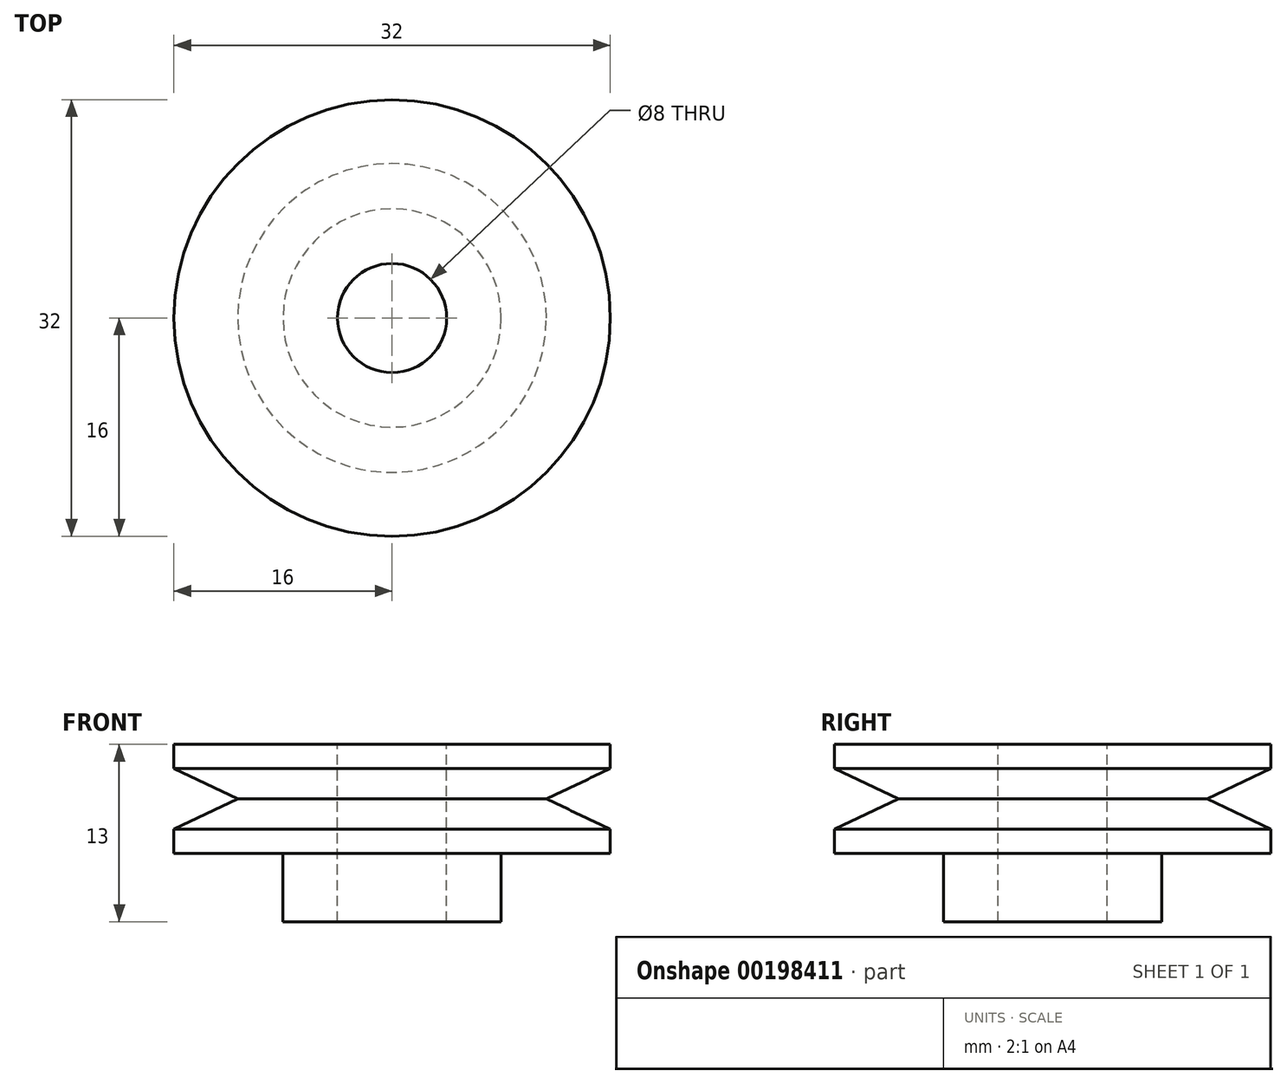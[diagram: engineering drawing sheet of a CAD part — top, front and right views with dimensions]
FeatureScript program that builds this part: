
annotation { "Feature Type Name" : "Feature", "Feature Type Description" : "" }
export const myFeature = defineFeature(function(context is Context, id is Id, definition is map)
    precondition{}
    {
        {
            var Q0;
            Q0=qCreatedBy(makeId("Front.planeOp"),FACE);
            var sketch = newSketch(context, id + "F0", { "sketchPlane" : qUnion([Q0])});
            skLineSegment(sketch, "E0", {"start": v(0, 0) * mm, "end": v(-8, 0) * mm});
            skLineSegment(sketch, "E1", {"start": v(-8, 0) * mm, "end": v(-8, 5) * mm});
            skLineSegment(sketch, "E2", {"start": v(-8, 5) * mm, "end": v(-16, 5) * mm});
            skLineSegment(sketch, "E3", {"start": v(-16, 5) * mm, "end": v(-16, 6.78) * mm});
            skLineSegment(sketch, "E4", {"start": v(-16, 13) * mm, "end": v(-8, 13) * mm});
            skLineSegment(sketch, "E5", {"start": v(0, 13) * mm, "end": v(0, 0) * mm});
            skLineSegment(sketch, "E6", {"start": v(-11.32, 9) * mm, "end": v(-16, 11.22) * mm});
            skPoint(sketch, "E6.startSnap0", {"position": v(-16, 9) * mm});
            skLineSegment(sketch, "E7.MirrorCS", {"start": v(-11.32, 9) * mm, "end": v(-16, 6.78) * mm});
            skPoint(sketch, "E8.orphan", {"position": v(-30.85, 18.27) * mm});
            skPoint(sketch, "E9.orphan", {"position": v(-30.85, -0.27) * mm});
            skLineSegment(sketch, "E10.trimOffspring", {"start": v(-16, 11.22) * mm, "end": v(-16, 13) * mm});
            skLineSegment(sketch, "E11", {"start": v(-8, 13) * mm, "end": v(0, 13) * mm});
            skPoint(sketch, "E12.orphan", {"position": v(0, 15) * mm});
            skSolve(sketch);
        }
        {
            var Q0;
            Q0=makeQuery(id+"F0.imprint","IMPRINT",FACE,{"disambiguationData":[TD([[makeQuery(id+"F0.imprint","IMPRINT",EDGE,{"derivedFrom":sQuery(id+"F0.wireOp",EDGE,"E0")}),-1.0]])]});
            var Q1;
            Q1=sQuery(id+"F0.wireOp",EDGE,"E5");
            revolve(context, id + "F1", {"entities" : qUnion([Q0]), "axis" : qUnion([Q1]), "revolveType" : RevolveType.FULL});
        }
        {
            var Q0;
            Q0=qCreatedBy(makeId("Top.planeOp"),FACE);
            var sketch = newSketch(context, id + "F2", { "sketchPlane" : qUnion([Q0])});
            skCircle(sketch, "E13", {"center": v(0, 0) * mm, "radius": 4 * mm});
            skSolve(sketch);
        }
        {
            var Q0;
            Q0 = qSketchRegion(id + "F2", true);
            extrude(context, id + "F3", {"entities" : qUnion([Q0]), "operationType" : NewBodyOperationType.REMOVE, "oppositeDirection" : true, "depth" : 25 * mm, "hasSecondDirection" : true, "secondDirectionOppositeDirection" : false, "secondDirectionDepth" : 25 * mm});
        }
    });
